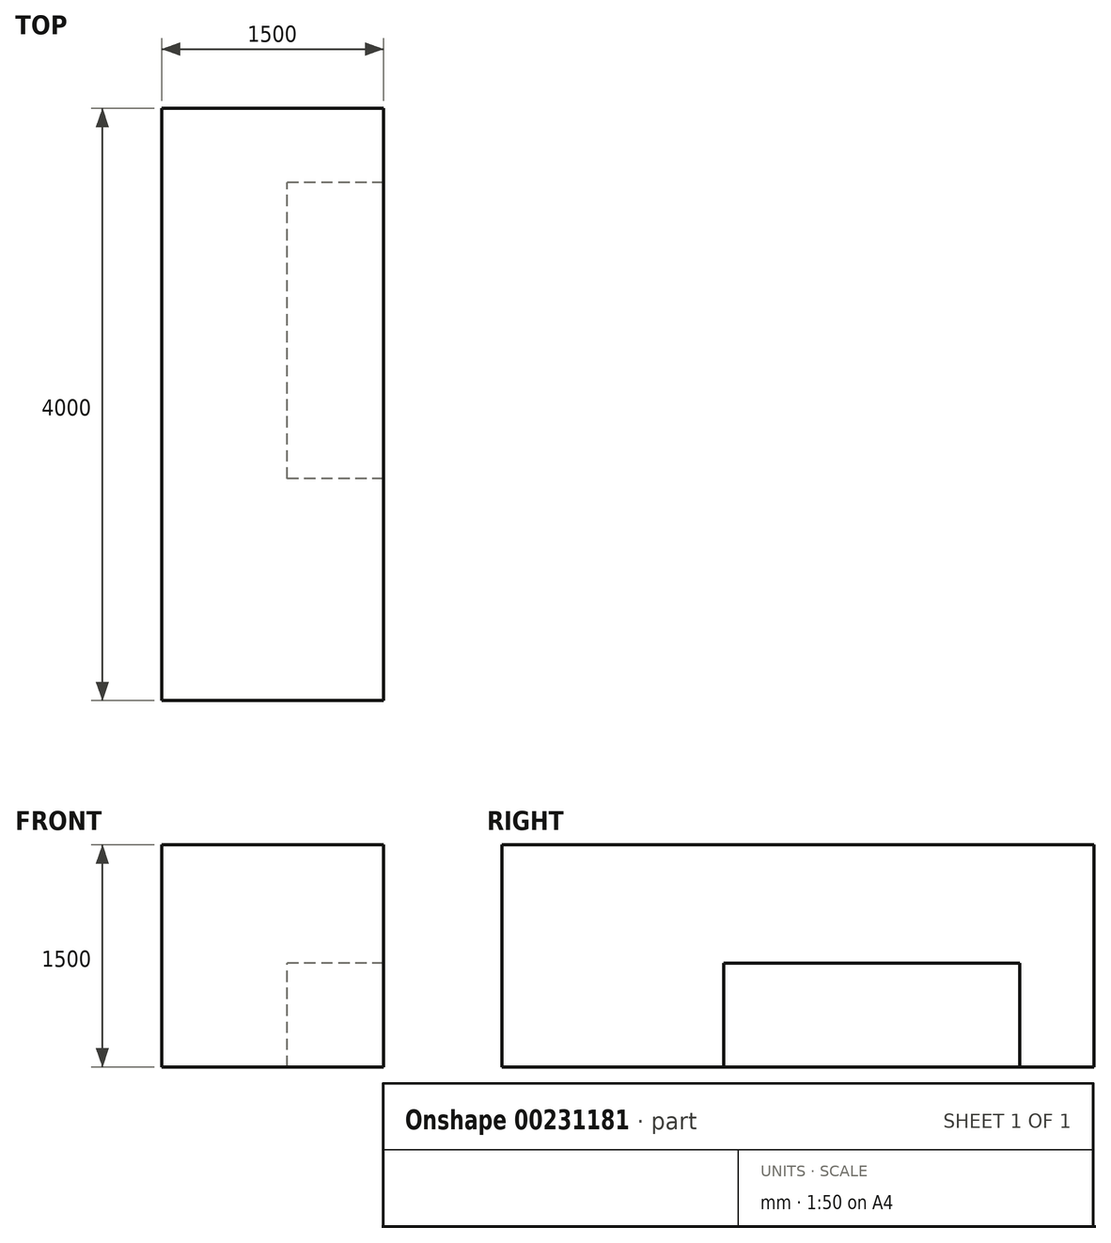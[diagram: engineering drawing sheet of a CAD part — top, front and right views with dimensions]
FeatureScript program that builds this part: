
annotation { "Feature Type Name" : "Feature", "Feature Type Description" : "" }
export const myFeature = defineFeature(function(context is Context, id is Id, definition is map)
    precondition{}
    {
        {
            var Q0;
            Q0=qCreatedBy(makeId("Front.planeOp"),FACE);
            var sketch = newSketch(context, id + "F0", { "sketchPlane" : qUnion([Q0])});
            skLineSegment(sketch, "E0.bottom", {"start": v(0, 0) * mm, "end": v(1500, 0) * mm});
            skLineSegment(sketch, "E0.top", {"start": v(0, 1500) * mm, "end": v(1500, 1500) * mm});
            skLineSegment(sketch, "E0.left", {"start": v(0, 0) * mm, "end": v(0, 1500) * mm});
            skLineSegment(sketch, "E0.right", {"start": v(1500, 0) * mm, "end": v(1500, 1500) * mm});
            skSolve(sketch);
        }
        {
            var Q0;
            Q0 = qSketchRegion(id + "F0", true);
            extrude(context, id + "F1", {"entities" : qUnion([Q0]), "oppositeDirection" : true, "depth" : 4000 * mm});
        }
        {
            var Q0;
            Q0=makeQuery(id+"F1.opExtrude","CAP_FACE",FACE,{"disambiguationData":[OSD([sQuery(id+"F0.wireOp",EDGE,"E0.bottom"),sQuery(id+"F0.wireOp",EDGE,"E0.top"),sQuery(id+"F0.wireOp",EDGE,"E0.left"),sQuery(id+"F0.wireOp",EDGE,"E0.right")])],"isStart":false});
            cPlane(context, id + "F2", {"entities" : qUnion([Q0]), "cplaneType" : CPlaneType.OFFSET, "offset" : 500 * mm, "oppositeDirection" : true, "width" : 150 * mm, "height" : 150 * mm});
        }
        {
            var Q0;
            Q0=qCreatedBy(id+"F2.planeOp",FACE);
            var sketch = newSketch(context, id + "F3", { "sketchPlane" : qUnion([Q0])});
            skLineSegment(sketch, "E1.bottom", {"start": v(-1500, 0) * mm, "end": v(-850, 0) * mm});
            skLineSegment(sketch, "E1.top", {"start": v(-1500, 700) * mm, "end": v(-850, 700) * mm});
            skLineSegment(sketch, "E1.left", {"start": v(-1500, 0) * mm, "end": v(-1500, 700) * mm});
            skLineSegment(sketch, "E1.right", {"start": v(-850, 0) * mm, "end": v(-850, 700) * mm});
            skSolve(sketch);
        }
        {
            var Q0;
            Q0=makeQuery(id+"F3.imprint","IMPRINT",FACE,{"disambiguationData":[TD([[makeQuery(id+"F3.imprint","IMPRINT",EDGE,{"derivedFrom":sQuery(id+"F3.wireOp",EDGE,"E1.bottom")}),1.0]])]});
            extrude(context, id + "F4", {"entities" : qUnion([Q0]), "operationType" : NewBodyOperationType.REMOVE, "oppositeDirection" : true, "depth" : 2000 * mm});
        }
    });
